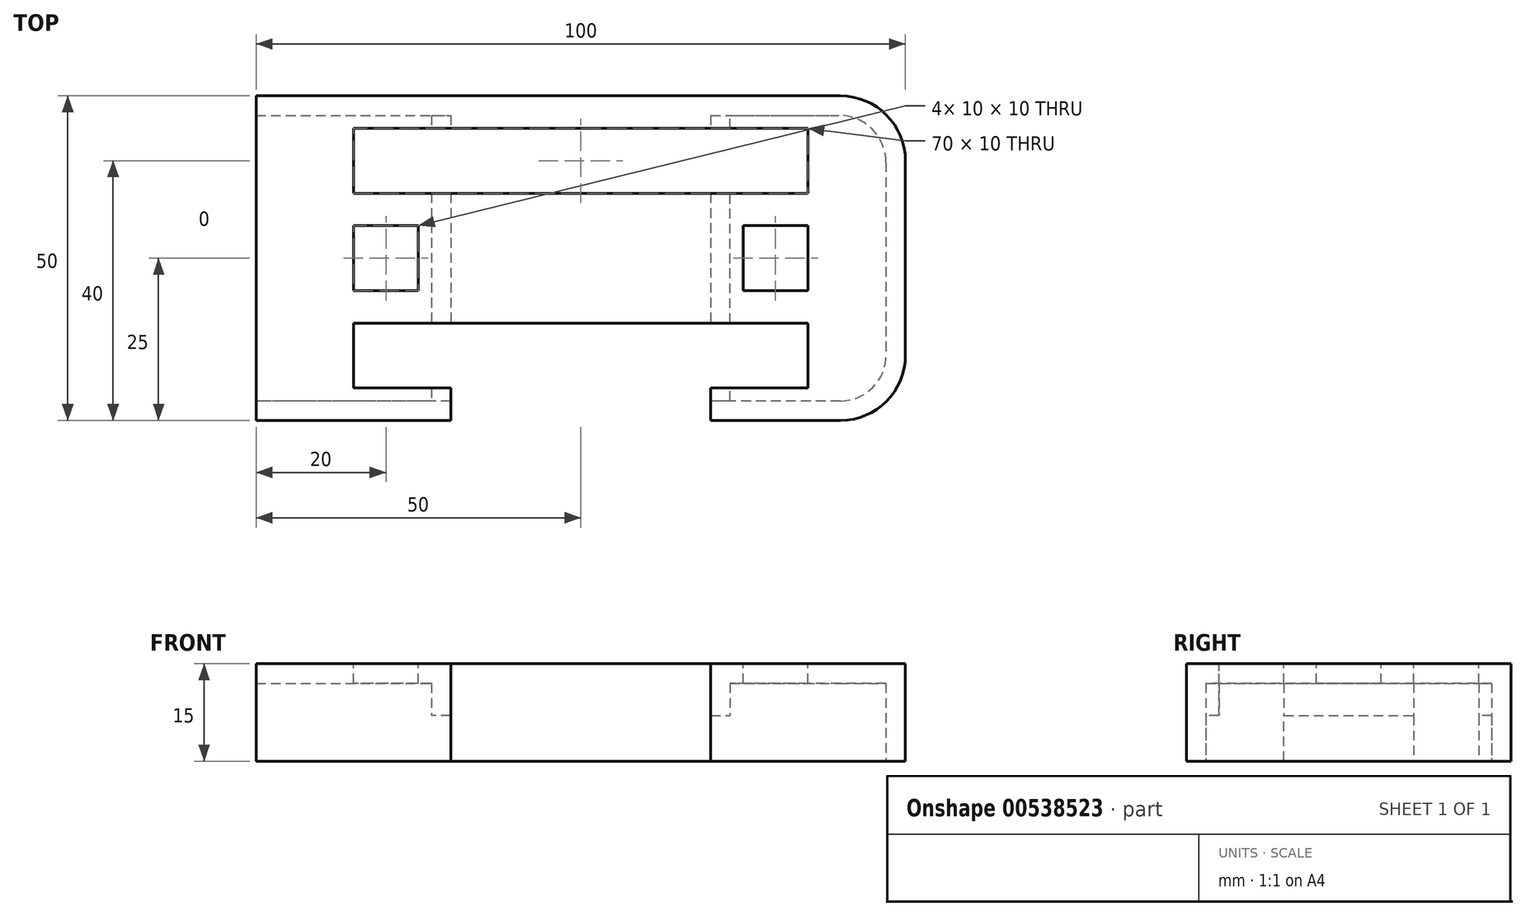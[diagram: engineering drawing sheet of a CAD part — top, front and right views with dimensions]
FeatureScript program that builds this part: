
annotation { "Feature Type Name" : "Feature", "Feature Type Description" : "" }
export const myFeature = defineFeature(function(context is Context, id is Id, definition is map)
    precondition{}
    {
        {
            var Q0;
            Q0=qCreatedBy(makeId("Top.planeOp"),FACE);
            var sketch = newSketch(context, id + "F0", { "sketchPlane" : qUnion([Q0])});
            skLineSegment(sketch, "E0.bottom", {"start": v(0, 0) * mm, "end": v(-100, 0) * mm});
            skLineSegment(sketch, "E0.top", {"start": v(0, 50) * mm, "end": v(-100, 50) * mm});
            skLineSegment(sketch, "E0.left", {"start": v(0, 0) * mm, "end": v(0, 50) * mm});
            skLineSegment(sketch, "E0.right", {"start": v(-100, 0) * mm, "end": v(-100, 50) * mm});
            skSolve(sketch);
        }
        {
            var Q0;
            Q0 = qSketchRegion(id + "F0", true);
            extrude(context, id + "F1", {"entities" : qUnion([Q0]), "depth" : 15 * mm, "offsetDistance" : 25 * mm});
        }
        {
            var Q0;
            Q0=makeQuery(id+"F1.opExtrude","CAP_FACE",FACE,{"disambiguationData":[OSD([sQuery(id+"F0.wireOp",EDGE,"E0.bottom"),sQuery(id+"F0.wireOp",EDGE,"E0.top"),sQuery(id+"F0.wireOp",EDGE,"E0.left"),sQuery(id+"F0.wireOp",EDGE,"E0.right")])],"isStart":false});
            var sketch = newSketch(context, id + "F2", { "sketchPlane" : qUnion([Q0])});
            skLineSegment(sketch, "E1", {"start": v(0, 50) * mm, "end": v(-15, 50) * mm});
            skLineSegment(sketch, "E2", {"start": v(0, 50) * mm, "end": v(0, 45) * mm});
            skLineSegment(sketch, "E3", {"start": v(-15, 50) * mm, "end": v(-25, 50) * mm});
            skLineSegment(sketch, "E4", {"start": v(-15, 50) * mm, "end": v(-35, 50) * mm});
            skLineSegment(sketch, "E5", {"start": v(-15, 50) * mm, "end": v(-15, 35) * mm});
            skLineSegment(sketch, "E6.bottom", {"start": v(-15, 35) * mm, "end": v(-25, 35) * mm});
            skLineSegment(sketch, "E6.top", {"start": v(-15, 45) * mm, "end": v(-25, 45) * mm});
            skLineSegment(sketch, "E6.left", {"start": v(-15, 35) * mm, "end": v(-15, 45) * mm});
            skLineSegment(sketch, "E6.right", {"start": v(-25, 35) * mm, "end": v(-25, 45) * mm});
            skLineSegment(sketch, "E7.bottom", {"start": v(-25, 35) * mm, "end": v(-85, 35) * mm});
            skLineSegment(sketch, "E7.top", {"start": v(-25, 45) * mm, "end": v(-85, 45) * mm});
            skLineSegment(sketch, "E7.right", {"start": v(-85, 35) * mm, "end": v(-85, 45) * mm});
            skLineSegment(sketch, "E8", {"start": v(-25, 45) * mm, "end": v(-35, 45) * mm});
            skLineSegment(sketch, "E9", {"start": v(-35, 45) * mm, "end": v(-45, 45) * mm});
            skLineSegment(sketch, "E10", {"start": v(-45, 45) * mm, "end": v(-55, 45) * mm});
            skLineSegment(sketch, "E11", {"start": v(-55, 45) * mm, "end": v(-65, 45) * mm});
            skLineSegment(sketch, "E12", {"start": v(-65, 45) * mm, "end": v(-75, 45) * mm});
            skLineSegment(sketch, "E13", {"start": v(-75, 45) * mm, "end": v(-75, 35) * mm});
            skLineSegment(sketch, "E14", {"start": v(-65, 45) * mm, "end": v(-65, 35) * mm});
            skLineSegment(sketch, "E15", {"start": v(-55, 45) * mm, "end": v(-55, 35) * mm});
            skLineSegment(sketch, "E16", {"start": v(-45, 45) * mm, "end": v(-45, 35) * mm});
            skLineSegment(sketch, "E17", {"start": v(-35, 45) * mm, "end": v(-35, 35) * mm});
            skLineSegment(sketch, "E18", {"start": v(-85, 35) * mm, "end": v(-85, 30) * mm});
            skLineSegment(sketch, "E19", {"start": v(-85, 30) * mm, "end": v(-85, 20) * mm});
            skLineSegment(sketch, "E20", {"start": v(-85, 20) * mm, "end": v(-85, 15) * mm});
            skLineSegment(sketch, "E21", {"start": v(-85, 15) * mm, "end": v(-85, 5) * mm});
            skLineSegment(sketch, "E22.bottom", {"start": v(-85, 30) * mm, "end": v(-75, 30) * mm});
            skLineSegment(sketch, "E22.top", {"start": v(-85, 20) * mm, "end": v(-75, 20) * mm});
            skLineSegment(sketch, "E22.right", {"start": v(-75, 30) * mm, "end": v(-75, 20) * mm});
            skLineSegment(sketch, "E23.bottom", {"start": v(-85, 15) * mm, "end": v(-75, 15) * mm});
            skLineSegment(sketch, "E23.top", {"start": v(-85, 5) * mm, "end": v(-75, 5) * mm});
            skLineSegment(sketch, "E23.right", {"start": v(-75, 15) * mm, "end": v(-75, 5) * mm});
            skLineSegment(sketch, "E24.bottom", {"start": v(-75, 15) * mm, "end": v(-15, 15) * mm});
            skLineSegment(sketch, "E24.top", {"start": v(-75, 5) * mm, "end": v(-15, 5) * mm});
            skLineSegment(sketch, "E24.right", {"start": v(-15, 15) * mm, "end": v(-15, 5) * mm});
            skLineSegment(sketch, "E25", {"start": v(-75, 5) * mm, "end": v(-65, 5) * mm});
            skLineSegment(sketch, "E26", {"start": v(-65, 5) * mm, "end": v(-55, 5) * mm});
            skLineSegment(sketch, "E27", {"start": v(-55, 5) * mm, "end": v(-45, 5) * mm});
            skLineSegment(sketch, "E28", {"start": v(-45, 5) * mm, "end": v(-35, 5) * mm});
            skLineSegment(sketch, "E29", {"start": v(-35, 5) * mm, "end": v(-25, 5) * mm});
            skLineSegment(sketch, "E30", {"start": v(-65, 5) * mm, "end": v(-65, 15) * mm});
            skLineSegment(sketch, "E31", {"start": v(-55, 5) * mm, "end": v(-55, 15) * mm});
            skLineSegment(sketch, "E32", {"start": v(-45, 5) * mm, "end": v(-45, 15) * mm});
            skLineSegment(sketch, "E33", {"start": v(-35, 5) * mm, "end": v(-35, 15) * mm});
            skLineSegment(sketch, "E34", {"start": v(-25, 5) * mm, "end": v(-25, 15) * mm});
            skLineSegment(sketch, "E35", {"start": v(-25, 15) * mm, "end": v(-25, 35) * mm});
            skLineSegment(sketch, "E36", {"start": v(-15, 15) * mm, "end": v(-15, 20) * mm});
            skLineSegment(sketch, "E37.bottom", {"start": v(-15, 20) * mm, "end": v(-25, 20) * mm});
            skLineSegment(sketch, "E37.top", {"start": v(-15, 30) * mm, "end": v(-25, 30) * mm});
            skLineSegment(sketch, "E37.left", {"start": v(-15, 20) * mm, "end": v(-15, 30) * mm});
            skLineSegment(sketch, "E37.right", {"start": v(-25, 20) * mm, "end": v(-25, 30) * mm});
            skSolve(sketch);
        }
        {
            var Q0;
            Q0=makeQuery(id+"F2.imprint","IMPRINT",FACE,{"disambiguationData":[TD([[makeQuery(id+"F2.imprint","IMPRINT",EDGE,{"derivedFrom":sQuery(id+"F2.wireOp",EDGE,"E6.bottom")}),-1.0]])]});
            var Q1;
            Q1=makeQuery(id+"F2.imprint","IMPRINT",FACE,{"disambiguationData":[TD([[makeQuery(id+"F2.imprint","IMPRINT",EDGE,{"derivedFrom":sQuery(id+"F2.wireOp",EDGE,"E23.bottom")}),-1.0]])]});
            var Q2;
            Q2=makeQuery(id+"F2.imprint","IMPRINT",FACE,{"disambiguationData":[TD([[makeQuery(id+"F2.imprint","IMPRINT",EDGE,{"derivedFrom":sQuery(id+"F2.wireOp",EDGE,"E24.top")}),1.0]])]});
            var Q3;
            Q3=makeQuery(id+"F2.imprint","IMPRINT",FACE,{"disambiguationData":[TD([[makeQuery(id+"F2.imprint","IMPRINT",EDGE,{"derivedFrom":sQuery(id+"F2.wireOp",EDGE,"E37.bottom")}),-1.0]])]});
            var Q4;
            Q4=makeQuery(id+"F2.imprint","IMPRINT",FACE,{"disambiguationData":[TD([[makeQuery(id+"F2.imprint","IMPRINT",EDGE,{"derivedFrom":sQuery(id+"F2.wireOp",EDGE,"E9")}),1.0]])]});
            var Q5;
            Q5=makeQuery(id+"F2.imprint","IMPRINT",FACE,{"disambiguationData":[TD([[makeQuery(id+"F2.imprint","IMPRINT",EDGE,{"derivedFrom":sQuery(id+"F2.wireOp",EDGE,"E11")}),1.0]])]});
            var Q6;
            Q6=makeQuery(id+"F2.imprint","IMPRINT",FACE,{"disambiguationData":[TD([[makeQuery(id+"F2.imprint","IMPRINT",EDGE,{"derivedFrom":sQuery(id+"F2.wireOp",EDGE,"E26")}),1.0]])]});
            var Q7;
            Q7=makeQuery(id+"F2.imprint","IMPRINT",FACE,{"disambiguationData":[TD([[makeQuery(id+"F2.imprint","IMPRINT",EDGE,{"derivedFrom":sQuery(id+"F2.wireOp",EDGE,"E28")}),1.0]])]});
            var Q8;
            Q8=makeQuery(id+"F2.imprint","IMPRINT",FACE,{"disambiguationData":[TD([[makeQuery(id+"F2.imprint","IMPRINT",EDGE,{"derivedFrom":sQuery(id+"F2.wireOp",EDGE,"E7.top")}),1.0]])]});
            var Q9;
            Q9=makeQuery(id+"F2.imprint","IMPRINT",FACE,{"disambiguationData":[TD([[makeQuery(id+"F2.imprint","IMPRINT",EDGE,{"derivedFrom":sQuery(id+"F2.wireOp",EDGE,"E22.bottom")}),-1.0]])]});
            extrude(context, id + "F3", {"entities" : qUnion([Q0, Q1, Q2, Q3, Q4, Q5, Q6, Q7, Q8, Q9]), "operationType" : NewBodyOperationType.REMOVE, "endBound" : BoundingType.UP_TO_NEXT, "oppositeDirection" : true, "depth" : 25 * mm, "offsetDistance" : 25 * mm});
        }
        {
            var Q0;
            Q0=makeQuery(id+"F1.opExtrude","SWEPT_EDGE",EDGE,{"disambiguationData":[OSD([sQuery(id+"F0.wireOp",EDGE,"E0.top"),sQuery(id+"F0.wireOp",EDGE,"E0.left")])]});
            fillet(context, id + "F4", {"entities" : qUnion([Q0]), "radius" : 10 * mm, "tangentPropagation" : true, "allowEdgeOverflow" : false});
        }
        {
            var Q0;
            Q0=makeQuery(id+"F1.opExtrude","SWEPT_EDGE",EDGE,{"disambiguationData":[OSD([sQuery(id+"F0.wireOp",EDGE,"E0.bottom"),sQuery(id+"F0.wireOp",EDGE,"E0.left")])]});
            fillet(context, id + "F5", {"entities" : qUnion([Q0]), "radius" : 10 * mm, "tangentPropagation" : true, "allowEdgeOverflow" : false});
        }
        {
            var Q0;
            Q0=makeQuery(id+"F1.opExtrude","SWEPT_FACE",FACE,{"disambiguationData":[OSD([sQuery(id+"F0.wireOp",EDGE,"E0.bottom")])]});
            var sketch = newSketch(context, id + "F6", { "sketchPlane" : qUnion([Q0])});
            skLineSegment(sketch, "E38", {"start": v(-100, 0) * mm, "end": v(-70, 0) * mm});
            skLineSegment(sketch, "E39", {"start": v(-70, 0) * mm, "end": v(-30, 0) * mm});
            skLineSegment(sketch, "E40", {"start": v(-30, 0) * mm, "end": v(-30, 15) * mm});
            skLineSegment(sketch, "E41", {"start": v(-30, 15) * mm, "end": v(-70, 15) * mm});
            skLineSegment(sketch, "E42", {"start": v(-70, 15) * mm, "end": v(-70, 0) * mm});
            skLineSegment(sketch, "E43", {"start": v(-30, 0) * mm, "end": v(-30, 10) * mm});
            skLineSegment(sketch, "E44", {"start": v(-30, 10) * mm, "end": v(-70, 10) * mm});
            skSolve(sketch);
        }
        {
            var Q0;
            Q0=makeQuery(id+"F6.imprint","IMPRINT",FACE,{"disambiguationData":[TD([[makeQuery(id+"F6.imprint","IMPRINT",EDGE,{"derivedFrom":sQuery(id+"F6.wireOp",EDGE,"E40")}),1.0]])]});
            extrude(context, id + "F7", {"entities" : qUnion([Q0]), "operationType" : NewBodyOperationType.REMOVE, "endBound" : BoundingType.UP_TO_NEXT, "oppositeDirection" : true, "depth" : 25 * mm, "offsetDistance" : 25 * mm});
        }
        {
            var Q0;
            Q0=makeQuery(id+"F1.opExtrude","CAP_FACE",FACE,{"disambiguationData":[OSD([sQuery(id+"F0.wireOp",EDGE,"E0.bottom"),sQuery(id+"F0.wireOp",EDGE,"E0.top"),sQuery(id+"F0.wireOp",EDGE,"E0.left"),sQuery(id+"F0.wireOp",EDGE,"E0.right")])],"isStart":true});
            var sketch = newSketch(context, id + "F8", { "sketchPlane" : qUnion([Q0])});
            skLineSegment(sketch, "E45", {"start": v(-30, -50) * mm, "end": v(-70, -50) * mm});
            skLineSegment(sketch, "E46", {"start": v(-100, 0) * mm, "end": v(-100, -3) * mm});
            skLineSegment(sketch, "E47", {"start": v(-100, -3) * mm, "end": v(-100, -47) * mm});
            skLineSegment(sketch, "E48", {"start": v(-100, -47) * mm, "end": v(-100, -50) * mm});
            skLineSegment(sketch, "E49", {"start": v(-100, -47) * mm, "end": v(-10.24, -47) * mm});
            skLineSegment(sketch, "E50", {"start": v(-3, -39.76) * mm, "end": v(-3, -10) * mm});
            skLineSegment(sketch, "E51", {"start": v(-10, -3) * mm, "end": v(-100, -3) * mm});
            skPoint(sketch, "E52.visualSharp", {"position": v(-3, -3) * mm});
            skArc(sketch, "E52.filletArc", {"start": v(-3, -10) * mm, "mid": v(-5.05, -5.05) * mm, "end": v(-10, -3) * mm});
            skPoint(sketch, "E53.visualSharp", {"position": v(-3, -47) * mm});
            skArc(sketch, "E53.filletArc", {"start": v(-10.24, -47) * mm, "mid": v(-5.12, -44.88) * mm, "end": v(-3, -39.76) * mm});
            skLineSegment(sketch, "E54", {"start": v(-30, -50) * mm, "end": v(-30, -47) * mm});
            skLineSegment(sketch, "E55.bottom", {"start": v(-30, -47) * mm, "end": v(-70, -47) * mm});
            skLineSegment(sketch, "E55.top", {"start": v(-30, -3) * mm, "end": v(-70, -3) * mm});
            skLineSegment(sketch, "E55.left", {"start": v(-30, -47) * mm, "end": v(-30, -3) * mm});
            skLineSegment(sketch, "E55.right", {"start": v(-70, -47) * mm, "end": v(-70, -3) * mm});
            skLineSegment(sketch, "E56", {"start": v(-100, -50) * mm, "end": v(-70, -50) * mm});
            skLineSegment(sketch, "E57", {"start": v(-30, -3) * mm, "end": v(-27, -3) * mm});
            skLineSegment(sketch, "E58", {"start": v(-27, -3) * mm, "end": v(-27, -47) * mm});
            skLineSegment(sketch, "E59", {"start": v(-27, -47) * mm, "end": v(-30, -47) * mm});
            skLineSegment(sketch, "E60", {"start": v(-70, -47) * mm, "end": v(-73, -47) * mm});
            skLineSegment(sketch, "E61", {"start": v(-73, -47) * mm, "end": v(-73, -3) * mm});
            skLineSegment(sketch, "E62", {"start": v(-73, -3) * mm, "end": v(-70, -3) * mm});
            skSolve(sketch);
        }
        {
            var Q0;
            {var subQ0=makeQuery(id+"F1.opExtrude","CAP_FACE",FACE,{"disambiguationData":[OSD([sQuery(id+"F0.wireOp",EDGE,"E0.bottom"),sQuery(id+"F0.wireOp",EDGE,"E0.top"),sQuery(id+"F0.wireOp",EDGE,"E0.left"),sQuery(id+"F0.wireOp",EDGE,"E0.right")])],"isStart":true});Q0=makeQuery(id+"F8.imprint","IMPRINT",FACE,{"disambiguationData":[TD([[makeQuery(id+"F8.imprint","IMPRINT",EDGE,{"derivedFrom":makeQuery(id+"F3.boolean.opBoolean","COPY",EDGE,{"derivedFrom":makeQuery(id+"F3.opExtrude","TWEAK_EDGE",EDGE,{"derivedFrom":[subQ0,makeQuery(id+"F2.imprint","IMPRINT",EDGE,{"derivedFrom":sQuery(id+"F2.wireOp",EDGE,"E6.bottom")})]})})}),-1.0]])]});}
            var Q1;
            {var subQ3=makeQuery(id+"F1.opExtrude","CAP_FACE",FACE,{"disambiguationData":[OSD([sQuery(id+"F0.wireOp",EDGE,"E0.bottom"),sQuery(id+"F0.wireOp",EDGE,"E0.top"),sQuery(id+"F0.wireOp",EDGE,"E0.left"),sQuery(id+"F0.wireOp",EDGE,"E0.right")])],"isStart":true});Q1=makeQuery(id+"F8.imprint","IMPRINT",FACE,{"disambiguationData":[TD([[makeQuery(id+"F8.imprint","IMPRINT",EDGE,{"derivedFrom":makeQuery(id+"F3.boolean.opBoolean","COPY",EDGE,{"derivedFrom":makeQuery(id+"F3.opExtrude","TWEAK_EDGE",EDGE,{"derivedFrom":[subQ3,makeQuery(id+"F2.imprint","IMPRINT",EDGE,{"derivedFrom":sQuery(id+"F2.wireOp",EDGE,"E9")})]})})}),1.0]])]});}
            var Q2;
            {var subQ3=makeQuery(id+"F1.opExtrude","CAP_FACE",FACE,{"disambiguationData":[OSD([sQuery(id+"F0.wireOp",EDGE,"E0.bottom"),sQuery(id+"F0.wireOp",EDGE,"E0.top"),sQuery(id+"F0.wireOp",EDGE,"E0.left"),sQuery(id+"F0.wireOp",EDGE,"E0.right")])],"isStart":true});Q2=makeQuery(id+"F8.imprint","IMPRINT",FACE,{"disambiguationData":[TD([[makeQuery(id+"F8.imprint","IMPRINT",EDGE,{"derivedFrom":makeQuery(id+"F3.boolean.opBoolean","COPY",EDGE,{"derivedFrom":makeQuery(id+"F3.opExtrude","TWEAK_EDGE",EDGE,{"derivedFrom":[subQ3,makeQuery(id+"F2.imprint","IMPRINT",EDGE,{"derivedFrom":sQuery(id+"F2.wireOp",EDGE,"E11")})]})})}),1.0]])]});}
            var Q3;
            {var subQ3=makeQuery(id+"F1.opExtrude","CAP_FACE",FACE,{"disambiguationData":[OSD([sQuery(id+"F0.wireOp",EDGE,"E0.bottom"),sQuery(id+"F0.wireOp",EDGE,"E0.top"),sQuery(id+"F0.wireOp",EDGE,"E0.left"),sQuery(id+"F0.wireOp",EDGE,"E0.right")])],"isStart":true});Q3=makeQuery(id+"F8.imprint","IMPRINT",FACE,{"disambiguationData":[TD([[makeQuery(id+"F8.imprint","IMPRINT",EDGE,{"derivedFrom":makeQuery(id+"F3.boolean.opBoolean","COPY",EDGE,{"derivedFrom":makeQuery(id+"F3.opExtrude","TWEAK_EDGE",EDGE,{"derivedFrom":[subQ3,makeQuery(id+"F2.imprint","IMPRINT",EDGE,{"derivedFrom":sQuery(id+"F2.wireOp",EDGE,"E7.top")})]})})}),1.0]])]});}
            var Q4;
            {var subQ0=makeQuery(id+"F1.opExtrude","CAP_FACE",FACE,{"disambiguationData":[OSD([sQuery(id+"F0.wireOp",EDGE,"E0.bottom"),sQuery(id+"F0.wireOp",EDGE,"E0.top"),sQuery(id+"F0.wireOp",EDGE,"E0.left"),sQuery(id+"F0.wireOp",EDGE,"E0.right")])],"isStart":true});Q4=makeQuery(id+"F8.imprint","IMPRINT",FACE,{"disambiguationData":[TD([[makeQuery(id+"F8.imprint","IMPRINT",EDGE,{"derivedFrom":makeQuery(id+"F3.boolean.opBoolean","COPY",EDGE,{"derivedFrom":makeQuery(id+"F3.opExtrude","TWEAK_EDGE",EDGE,{"derivedFrom":[subQ0,makeQuery(id+"F2.imprint","IMPRINT",EDGE,{"derivedFrom":sQuery(id+"F2.wireOp",EDGE,"E22.bottom")})]})})}),-1.0]])]});}
            var Q5;
            {var subQ0=makeQuery(id+"F1.opExtrude","CAP_FACE",FACE,{"disambiguationData":[OSD([sQuery(id+"F0.wireOp",EDGE,"E0.bottom"),sQuery(id+"F0.wireOp",EDGE,"E0.top"),sQuery(id+"F0.wireOp",EDGE,"E0.left"),sQuery(id+"F0.wireOp",EDGE,"E0.right")])],"isStart":true});Q5=makeQuery(id+"F8.imprint","IMPRINT",FACE,{"disambiguationData":[TD([[makeQuery(id+"F8.imprint","IMPRINT",EDGE,{"derivedFrom":makeQuery(id+"F3.boolean.opBoolean","COPY",EDGE,{"derivedFrom":makeQuery(id+"F3.opExtrude","TWEAK_EDGE",EDGE,{"derivedFrom":[subQ0,makeQuery(id+"F2.imprint","IMPRINT",EDGE,{"derivedFrom":sQuery(id+"F2.wireOp",EDGE,"E23.bottom")})]})})}),-1.0]])]});}
            var Q6;
            {var subQ3=makeQuery(id+"F1.opExtrude","CAP_FACE",FACE,{"disambiguationData":[OSD([sQuery(id+"F0.wireOp",EDGE,"E0.bottom"),sQuery(id+"F0.wireOp",EDGE,"E0.top"),sQuery(id+"F0.wireOp",EDGE,"E0.left"),sQuery(id+"F0.wireOp",EDGE,"E0.right")])],"isStart":true});Q6=makeQuery(id+"F8.imprint","IMPRINT",FACE,{"disambiguationData":[TD([[makeQuery(id+"F8.imprint","IMPRINT",EDGE,{"derivedFrom":makeQuery(id+"F3.boolean.opBoolean","COPY",EDGE,{"derivedFrom":makeQuery(id+"F3.opExtrude","TWEAK_EDGE",EDGE,{"derivedFrom":[subQ3,makeQuery(id+"F2.imprint","IMPRINT",EDGE,{"derivedFrom":sQuery(id+"F2.wireOp",EDGE,"E26")})]})})}),1.0]])]});}
            var Q7;
            {var subQ3=makeQuery(id+"F1.opExtrude","CAP_FACE",FACE,{"disambiguationData":[OSD([sQuery(id+"F0.wireOp",EDGE,"E0.bottom"),sQuery(id+"F0.wireOp",EDGE,"E0.top"),sQuery(id+"F0.wireOp",EDGE,"E0.left"),sQuery(id+"F0.wireOp",EDGE,"E0.right")])],"isStart":true});Q7=makeQuery(id+"F8.imprint","IMPRINT",FACE,{"disambiguationData":[TD([[makeQuery(id+"F8.imprint","IMPRINT",EDGE,{"derivedFrom":makeQuery(id+"F3.boolean.opBoolean","COPY",EDGE,{"derivedFrom":makeQuery(id+"F3.opExtrude","TWEAK_EDGE",EDGE,{"derivedFrom":[subQ3,makeQuery(id+"F2.imprint","IMPRINT",EDGE,{"derivedFrom":sQuery(id+"F2.wireOp",EDGE,"E28")})]})})}),1.0]])]});}
            var Q8;
            {var subQ3=makeQuery(id+"F1.opExtrude","CAP_FACE",FACE,{"disambiguationData":[OSD([sQuery(id+"F0.wireOp",EDGE,"E0.bottom"),sQuery(id+"F0.wireOp",EDGE,"E0.top"),sQuery(id+"F0.wireOp",EDGE,"E0.left"),sQuery(id+"F0.wireOp",EDGE,"E0.right")])],"isStart":true});Q8=makeQuery(id+"F8.imprint","IMPRINT",FACE,{"disambiguationData":[TD([[makeQuery(id+"F8.imprint","IMPRINT",EDGE,{"derivedFrom":makeQuery(id+"F3.boolean.opBoolean","COPY",EDGE,{"derivedFrom":makeQuery(id+"F3.opExtrude","TWEAK_EDGE",EDGE,{"derivedFrom":[subQ3,makeQuery(id+"F2.imprint","IMPRINT",EDGE,{"derivedFrom":sQuery(id+"F2.wireOp",EDGE,"E24.top")})]})})}),1.0]])]});}
            var Q9;
            {var subQ0=makeQuery(id+"F1.opExtrude","CAP_FACE",FACE,{"disambiguationData":[OSD([sQuery(id+"F0.wireOp",EDGE,"E0.bottom"),sQuery(id+"F0.wireOp",EDGE,"E0.top"),sQuery(id+"F0.wireOp",EDGE,"E0.left"),sQuery(id+"F0.wireOp",EDGE,"E0.right")])],"isStart":true});Q9=makeQuery(id+"F8.imprint","IMPRINT",FACE,{"disambiguationData":[TD([[makeQuery(id+"F8.imprint","IMPRINT",EDGE,{"derivedFrom":makeQuery(id+"F3.boolean.opBoolean","COPY",EDGE,{"derivedFrom":makeQuery(id+"F3.opExtrude","TWEAK_EDGE",EDGE,{"derivedFrom":[subQ0,makeQuery(id+"F2.imprint","IMPRINT",EDGE,{"derivedFrom":sQuery(id+"F2.wireOp",EDGE,"E37.bottom")})]})})}),-1.0]])]});}
            var Q10;
            Q10=makeQuery(id+"F8.imprint","IMPRINT",FACE,{"disambiguationData":[TD([[makeQuery(id+"F8.imprint","IMPRINT",EDGE,{"derivedFrom":sQuery(id+"F8.wireOp",EDGE,"E55.left")}),-1.0]])]});
            var Q11;
            Q11=makeQuery(id+"F8.imprint","IMPRINT",FACE,{"disambiguationData":[TD([[makeQuery(id+"F8.imprint","IMPRINT",EDGE,{"derivedFrom":sQuery(id+"F8.wireOp",EDGE,"E55.right")}),1.0]])]});
            var Q12;
            Q12=makeQuery(id+"F8.imprint","IMPRINT",FACE,{"disambiguationData":[TD([[makeQuery(id+"F8.imprint","IMPRINT",EDGE,{"derivedFrom":sQuery(id+"F8.wireOp",EDGE,"E50")}),1.0]])]});
            var Q13;
            {var subQ4=sQuery(id+"F8.wireOp",EDGE,"E47");Q13=makeQuery(id+"F8.imprint","IMPRINT",FACE,{"disambiguationData":[TD([[makeQuery(id+"F8.imprint","IMPRINT",EDGE,{"derivedFrom":subQ4}),1.0]])]});}
            var Q14;
            Q14=makeQuery(id+"F8.imprint","IMPRINT",FACE,{"disambiguationData":[TD([[makeQuery(id+"F8.imprint","IMPRINT",EDGE,{"derivedFrom":sQuery(id+"F8.wireOp",EDGE,"E55.bottom")}),-1.0]])]});
            extrude(context, id + "F9", {"entities" : qUnion([Q0, Q1, Q2, Q3, Q4, Q5, Q6, Q7, Q8, Q9, Q10, Q11, Q12, Q13, Q14]), "operationType" : NewBodyOperationType.REMOVE, "oppositeDirection" : true, "depth" : 7 * mm, "offsetDistance" : 25 * mm});
        }
        {
            var Q0;
            {var subQ4=sQuery(id+"F8.wireOp",EDGE,"E47");Q0=makeQuery(id+"F8.imprint","IMPRINT",FACE,{"disambiguationData":[TD([[makeQuery(id+"F8.imprint","IMPRINT",EDGE,{"derivedFrom":subQ4}),1.0]])]});}
            var Q1;
            Q1=makeQuery(id+"F8.imprint","IMPRINT",FACE,{"disambiguationData":[TD([[makeQuery(id+"F8.imprint","IMPRINT",EDGE,{"derivedFrom":sQuery(id+"F8.wireOp",EDGE,"E50")}),1.0]])]});
            extrude(context, id + "F10", {"entities" : qUnion([Q0, Q1]), "operationType" : NewBodyOperationType.REMOVE, "oppositeDirection" : true, "depth" : 12 * mm, "offsetDistance" : 25 * mm});
        }
    });
